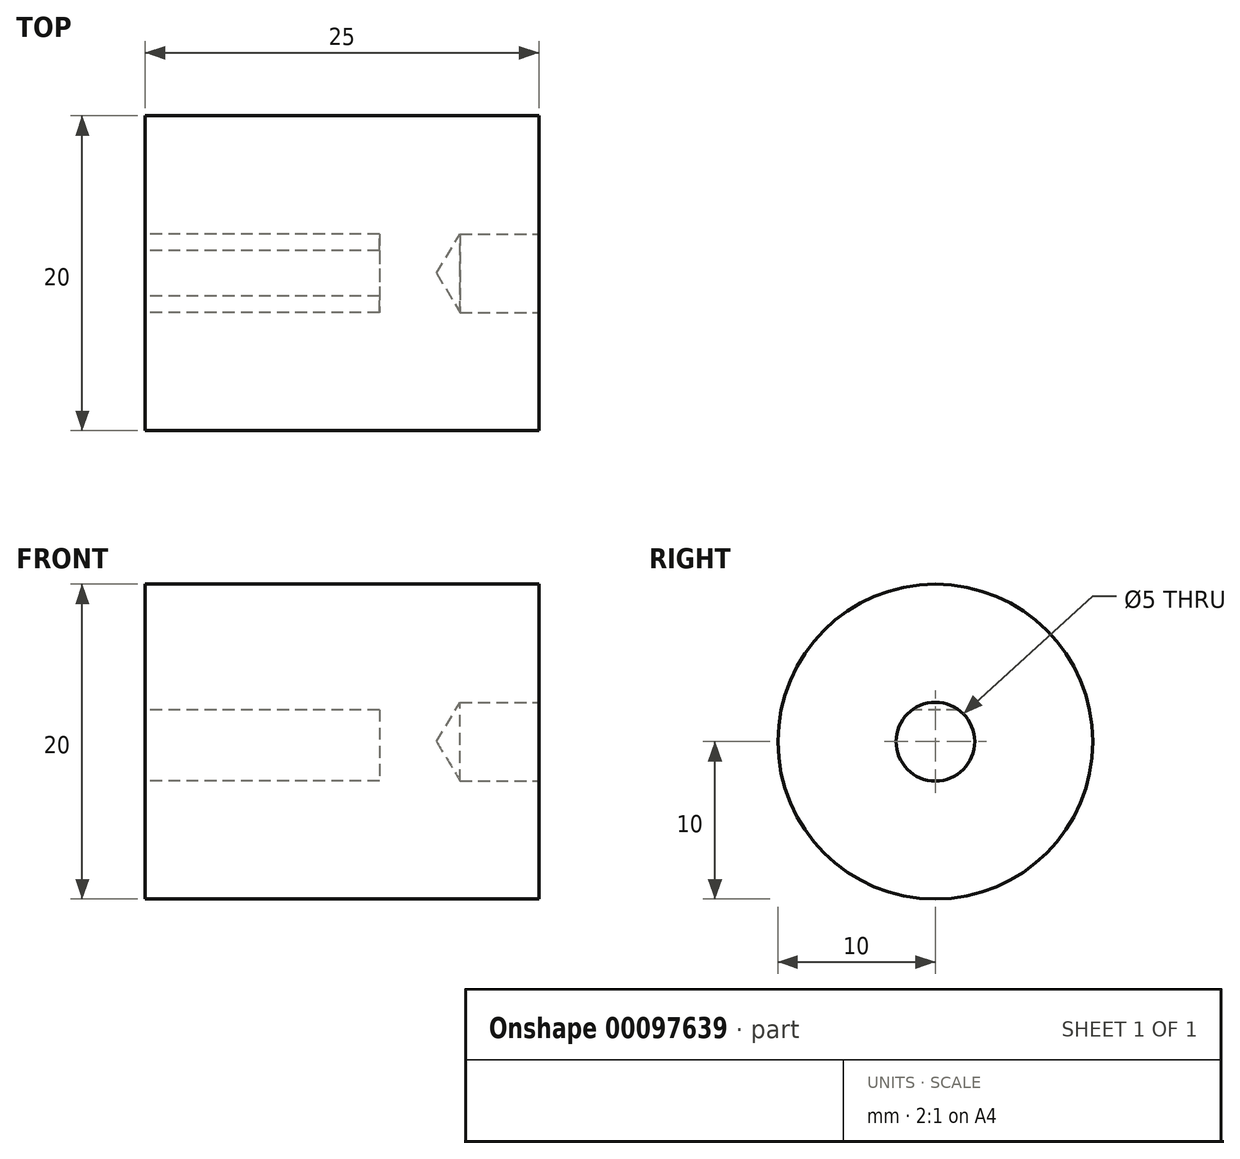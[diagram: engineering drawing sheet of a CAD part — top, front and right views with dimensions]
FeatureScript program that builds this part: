
annotation { "Feature Type Name" : "Feature", "Feature Type Description" : "" }
export const myFeature = defineFeature(function(context is Context, id is Id, definition is map)
    precondition{}
    {
        {
            var Q0;
            Q0=qCreatedBy(makeId("Right.planeOp"),FACE);
            var sketch = newSketch(context, id + "F0", { "sketchPlane" : qUnion([Q0])});
            skCircle(sketch, "E0", {"center": v(0, 0) * mm, "radius": 10 * mm});
            skCircle(sketch, "E1", {"center": v(0, 0) * mm, "radius": 2.5 * mm});
            skSolve(sketch);
        }
        {
            var Q0;
            Q0=makeQuery(id+"F0.imprint","IMPRINT",FACE,{"disambiguationData":[TD([[makeQuery(id+"F0.imprint","IMPRINT",EDGE,{"derivedFrom":sQuery(id+"F0.wireOp",EDGE,"E0")}),1.0]])]});
            var Q1;
            Q1=makeQuery(id+"F0.imprint","IMPRINT",FACE,{"disambiguationData":[TD([[makeQuery(id+"F0.imprint","IMPRINT",EDGE,{"derivedFrom":sQuery(id+"F0.wireOp",EDGE,"E1")}),1.0]])]});
            extrude(context, id + "F2", {"entities" : qUnion([Q0, Q1]), "endBound" : BoundingType.SYMMETRIC, "depth" : 25 * mm});
        }
        {
            var Q0;
            Q0=makeQuery(id+"F2.opExtrude","CAP_FACE",FACE,{"disambiguationData":[OSD([sQuery(id+"F0.wireOp",EDGE,"E0"),sQuery(id+"F0.wireOp",EDGE,"E1")])],"isStart":false});
            var sketch = newSketch(context, id + "F1", { "sketchPlane" : qUnion([Q0])});
            skPoint(sketch, "E2", {"position": v(0, 0) * mm});
            skSolve(sketch);
        }
        {
            var Q0;
            Q0=sQuery(id+"F1.wireOp",VERTEX,"E2");
            var Q1;
            Q1=makeQuery(id+"F2.opExtrude","SWEPT_BODY",BODY,{"disambiguationData":[OSD([sQuery(id+"F0.wireOp",EDGE,"E0")])]});
            hole(context, id + "F3", {"style" : HoleStyle.SIMPLE, "endStyle" : HoleEndStyle.BLIND, "standardTappedOrClearance" : lookupTablePath({ "standard" : "ISO" }), "standardBlindInLast" : lookupTablePath({ "standard" : "ISO" }), "holeDiameter" : 5 * mm, "holeDepth" : 5 * mm, "locations" : qUnion([Q0]), "scope" : qUnion([Q1])});
        }
        {
            var Q0;
            Q0=makeQuery(id+"F2.opExtrude","CAP_FACE",FACE,{"disambiguationData":[OSD([sQuery(id+"F0.wireOp",EDGE,"E0")])],"isStart":true});
            var sketch = newSketch(context, id + "F4", { "sketchPlane" : qUnion([Q0])});
            skArc(sketch, "E3", {"start": v(-1.46, 2.03) * mm, "mid": v(0, -2.5) * mm, "end": v(1.46, 2.03) * mm});
            skLineSegment(sketch, "E4", {"start": v(-1.46, 2.03) * mm, "end": v(1.46, 2.03) * mm});
            skSolve(sketch);
        }
        {
            var Q0;
            Q0=makeQuery(id+"F4.imprint","IMPRINT",FACE,{"disambiguationData":[TD([[makeQuery(id+"F4.imprint","IMPRINT",EDGE,{"derivedFrom":sQuery(id+"F4.wireOp",EDGE,"E3")}),1.0]])]});
            extrude(context, id + "F5", {"entities" : qUnion([Q0]), "operationType" : NewBodyOperationType.REMOVE, "oppositeDirection" : true, "depth" : 14.87 * mm});
        }
    });
